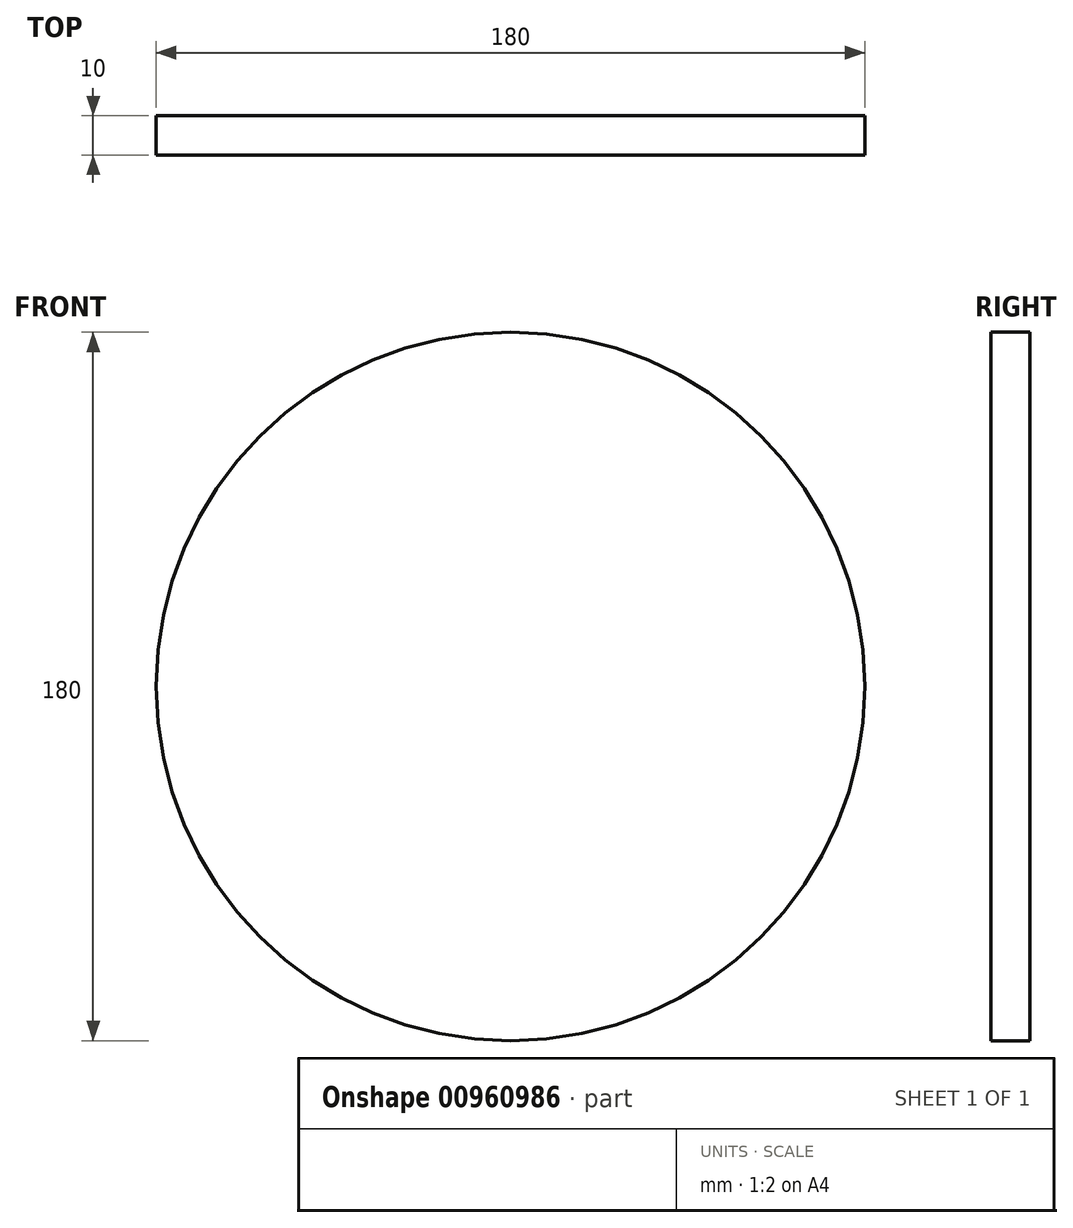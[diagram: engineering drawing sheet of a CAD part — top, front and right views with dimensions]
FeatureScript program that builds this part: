
annotation { "Feature Type Name" : "Feature", "Feature Type Description" : "" }
export const myFeature = defineFeature(function(context is Context, id is Id, definition is map)
    precondition{}
    {
        {
            var Q0;
            Q0=qCreatedBy(makeId("Front.planeOp"),FACE);
            var sketch = newSketch(context, id + "F0", { "sketchPlane" : qUnion([Q0])});
            skCircle(sketch, "E0", {"center": v(0, 0) * mm, "radius": 90 * mm});
            skLineSegment(sketch, "E1", {"start": v(0, 0) * mm, "end": v(0, -90) * mm, "construction": true});
            skLineSegment(sketch, "E2", {"start": v(0, -90) * mm, "end": v(0, -80) * mm, "construction": true});
            skLineSegment(sketch, "E3", {"start": v(0, -80) * mm, "end": v(-40, -80) * mm, "construction": true});
            skLineSegment(sketch, "E4.bottom", {"start": v(-40, -80) * mm, "end": v(40, -80) * mm, "construction": true});
            skLineSegment(sketch, "E4.top", {"start": v(-40, -48) * mm, "end": v(40, -48) * mm, "construction": true});
            skLineSegment(sketch, "E4.left", {"start": v(-40, -80) * mm, "end": v(-40, -48) * mm, "construction": true});
            skLineSegment(sketch, "E4.right", {"start": v(40, -80) * mm, "end": v(40, -48) * mm, "construction": true});
            skSolve(sketch);
        }
        {
            var Q0;
            Q0=makeQuery(id+"F0.imprint","IMPRINT",FACE,{"disambiguationData":[TD([[makeQuery(id+"F0.imprint","IMPRINT",EDGE,{"derivedFrom":sQuery(id+"F0.wireOp",EDGE,"E0")}),1.0]])]});
            extrude(context, id + "F1", {"entities" : qUnion([Q0]), "depth" : 10 * mm, "offsetDistance" : 25 * mm});
        }
    });
